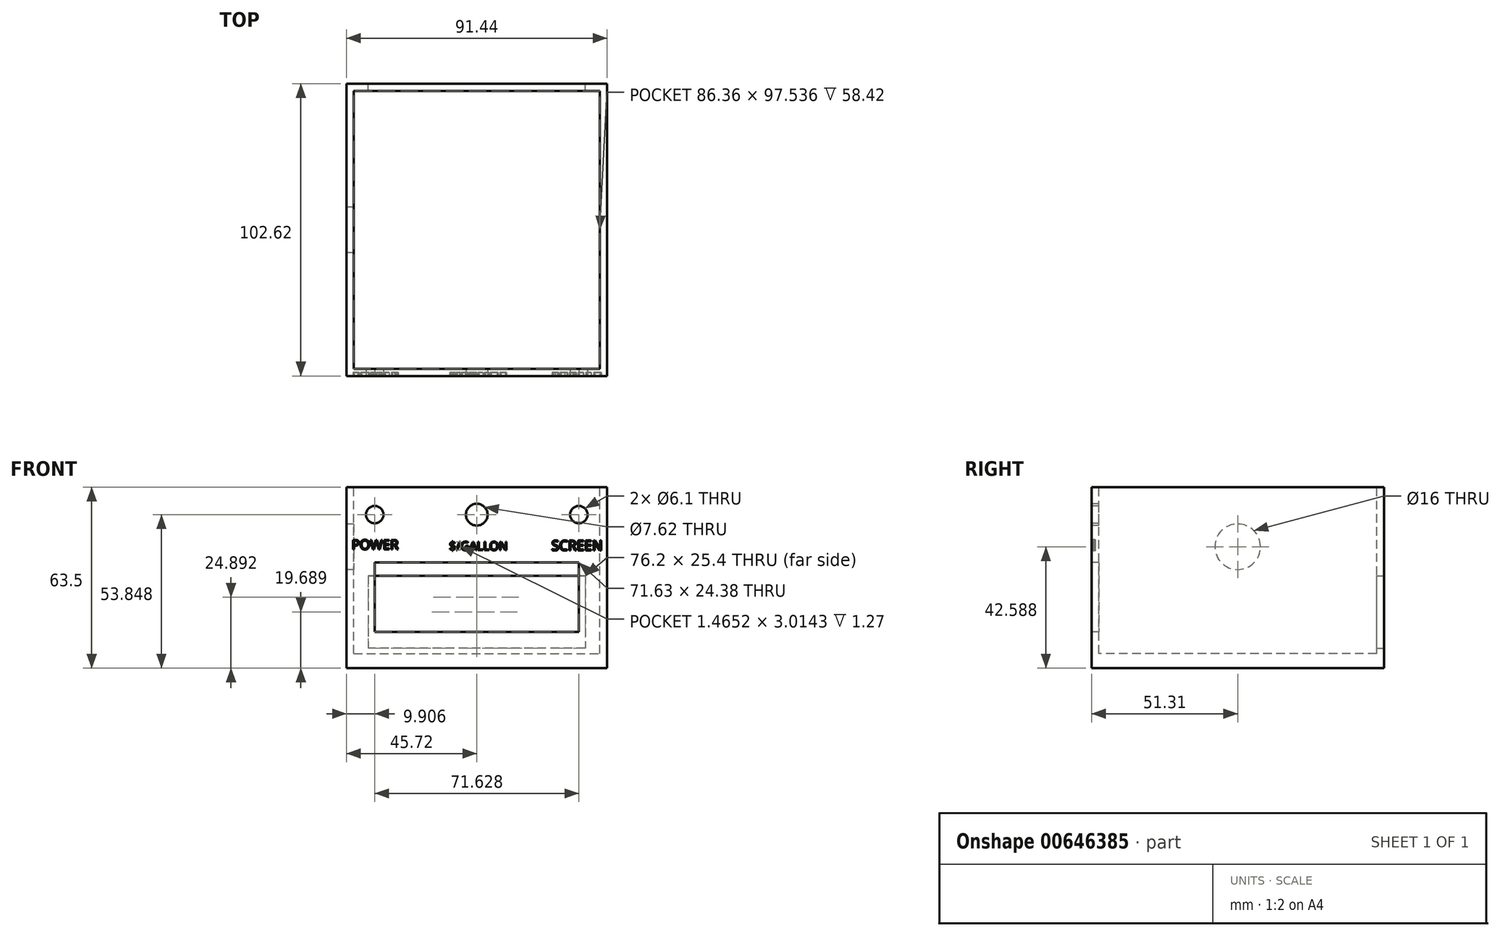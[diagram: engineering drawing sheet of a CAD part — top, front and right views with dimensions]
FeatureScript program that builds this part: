
annotation { "Feature Type Name" : "Feature", "Feature Type Description" : "" }
export const myFeature = defineFeature(function(context is Context, id is Id, definition is map)
    precondition{}
    {
        {
            var Q0;
            Q0=qCreatedBy(makeId("Top.planeOp"),FACE);
            var sketch = newSketch(context, id + "F0", { "sketchPlane" : qUnion([Q0])});
            skLineSegment(sketch, "E0.bottom", {"start": v(-45.72, 51.3) * mm, "end": v(45.72, 51.3) * mm});
            skLineSegment(sketch, "E0.top", {"start": v(-45.72, -51.3) * mm, "end": v(45.72, -51.3) * mm});
            skLineSegment(sketch, "E0.left", {"start": v(-45.72, 51.3) * mm, "end": v(-45.72, -51.3) * mm});
            skLineSegment(sketch, "E0.right", {"start": v(45.72, 51.3) * mm, "end": v(45.72, -51.3) * mm});
            skSolve(sketch);
        }
        {
            var Q0;
            Q0=makeQuery(id+"F0.imprint","IMPRINT",FACE,{"disambiguationData":[TD([[makeQuery(id+"F0.imprint","IMPRINT",EDGE,{"derivedFrom":sQuery(id+"F0.wireOp",EDGE,"E0.bottom")}),-1.0]])]});
            extrude(context, id + "F1", {"entities" : qUnion([Q0]), "depth" : 63.5 * mm, "offsetDistance" : 25.4 * mm});
        }
        {
            var Q0;
            Q0=makeQuery(id+"F1.opExtrude","CAP_FACE",FACE,{"disambiguationData":[OSD([sQuery(id+"F0.wireOp",EDGE,"E0.bottom"),sQuery(id+"F0.wireOp",EDGE,"E0.top"),sQuery(id+"F0.wireOp",EDGE,"E0.left"),sQuery(id+"F0.wireOp",EDGE,"E0.right")])],"isStart":false});
            var sketch = newSketch(context, id + "F2", { "sketchPlane" : qUnion([Q0])});
            skLineSegment(sketch, "E1.bottom", {"start": v(-43.18, 48.77) * mm, "end": v(43.18, 48.77) * mm});
            skLineSegment(sketch, "E1.top", {"start": v(-43.18, -48.77) * mm, "end": v(43.18, -48.77) * mm});
            skLineSegment(sketch, "E1.left", {"start": v(-43.18, 48.77) * mm, "end": v(-43.18, -48.77) * mm});
            skLineSegment(sketch, "E1.right", {"start": v(43.18, 48.77) * mm, "end": v(43.18, -48.77) * mm});
            skSolve(sketch);
        }
        {
            var Q0;
            Q0=makeQuery(id+"F2.imprint","IMPRINT",FACE,{"disambiguationData":[TD([[makeQuery(id+"F2.imprint","IMPRINT",EDGE,{"derivedFrom":sQuery(id+"F2.wireOp",EDGE,"E1.bottom")}),-1.0]])]});
            extrude(context, id + "F3", {"entities" : qUnion([Q0]), "operationType" : NewBodyOperationType.REMOVE, "oppositeDirection" : true, "depth" : 58.42 * mm, "offsetDistance" : 25.4 * mm});
        }
        {
            var Q0;
            Q0=makeQuery(id+"F1.opExtrude","SWEPT_FACE",FACE,{"disambiguationData":[OSD([sQuery(id+"F0.wireOp",EDGE,"E0.top")])]});
            var sketch = newSketch(context, id + "F4", { "sketchPlane" : qUnion([Q0])});
            skLineSegment(sketch, "E2.bottom", {"start": v(-35.81, 37.08) * mm, "end": v(35.81, 37.08) * mm});
            skLineSegment(sketch, "E2.top", {"start": v(-35.81, 12.7) * mm, "end": v(35.81, 12.7) * mm});
            skLineSegment(sketch, "E2.left", {"start": v(-35.81, 37.08) * mm, "end": v(-35.81, 12.7) * mm});
            skLineSegment(sketch, "E2.right", {"start": v(35.81, 37.08) * mm, "end": v(35.81, 12.7) * mm});
            skSolve(sketch);
        }
        {
            var Q0;
            Q0=makeQuery(id+"F4.imprint","IMPRINT",FACE,{"disambiguationData":[TD([[makeQuery(id+"F4.imprint","IMPRINT",EDGE,{"derivedFrom":sQuery(id+"F4.wireOp",EDGE,"E2.bottom")}),-1.0]])]});
            extrude(context, id + "F5", {"entities" : qUnion([Q0]), "operationType" : NewBodyOperationType.REMOVE, "oppositeDirection" : true, "depth" : 25.4 * mm, "offsetDistance" : 25.4 * mm});
        }
        {
            var Q0;
            Q0=makeQuery(id+"F1.opExtrude","SWEPT_FACE",FACE,{"disambiguationData":[OSD([sQuery(id+"F0.wireOp",EDGE,"E0.top")])]});
            var sketch = newSketch(context, id + "F6", { "sketchPlane" : qUnion([Q0])});
            skCircle(sketch, "E3", {"center": v(0, 53.85) * mm, "radius": 3.81 * mm});
            skPoint(sketch, "E3.centerSnap0", {"position": v(0, 37.08) * mm});
            skCircle(sketch, "E4", {"center": v(-35.81, 53.85) * mm, "radius": 3.05 * mm});
            skCircle(sketch, "E5", {"center": v(35.81, 53.85) * mm, "radius": 3.05 * mm});
            skSolve(sketch);
        }
        {
            var Q0;
            Q0=makeQuery(id+"F6.imprint","IMPRINT",FACE,{"disambiguationData":[TD([[makeQuery(id+"F6.imprint","IMPRINT",EDGE,{"derivedFrom":sQuery(id+"F6.wireOp",EDGE,"E4")}),1.0]])]});
            var Q1;
            Q1=makeQuery(id+"F6.imprint","IMPRINT",FACE,{"disambiguationData":[TD([[makeQuery(id+"F6.imprint","IMPRINT",EDGE,{"derivedFrom":sQuery(id+"F6.wireOp",EDGE,"E3")}),1.0]])]});
            var Q2;
            Q2=makeQuery(id+"F6.imprint","IMPRINT",FACE,{"disambiguationData":[TD([[makeQuery(id+"F6.imprint","IMPRINT",EDGE,{"derivedFrom":sQuery(id+"F6.wireOp",EDGE,"E5")}),1.0]])]});
            extrude(context, id + "F7", {"entities" : qUnion([Q0, Q1, Q2]), "operationType" : NewBodyOperationType.REMOVE, "oppositeDirection" : true, "depth" : 7.62 * mm, "offsetDistance" : 25.4 * mm});
        }
        {
            var Q0;
            Q0=makeQuery(id+"F1.opExtrude","SWEPT_FACE",FACE,{"disambiguationData":[OSD([sQuery(id+"F0.wireOp",EDGE,"E0.top")])]});
            var sketch = newSketch(context, id + "F8", { "sketchPlane" : qUnion([Q0])});
            skText(sketch, "E6", { "text": "POWER", "fontName": "OpenSans-Regular.ttf"});
            const initialGuessF8  = {"E6": [-0.04393, 0.04162, 1, 0, 0.0034]};
            skSetInitialGuess(sketch, initialGuessF8);
            skSolve(sketch);
        }
        {
            var Q0;
            Q0 = qSketchRegion(id + "F8", true);
            extrude(context, id + "F9", {"entities" : qUnion([Q0]), "operationType" : NewBodyOperationType.REMOVE, "oppositeDirection" : true, "depth" : 1.27 * mm, "offsetDistance" : 25.4 * mm});
        }
        {
            var Q0;
            {var subQ1=sQuery(id+"F0.wireOp",EDGE,"E0.left");var subQ2=sQuery(id+"F0.wireOp",EDGE,"E0.top");Q0=makeQuery(id+"F9.boolean.opBoolean","SPLIT",FACE,{"disambiguationData":[TD([makeQuery(id+"F1.opExtrude","SWEPT_FACE",FACE,{"disambiguationData":[OSD([subQ1])]})])],"derivedFrom":makeQuery(id+"F1.opExtrude","SWEPT_FACE",FACE,{"disambiguationData":[OSD([subQ2])]})});}
            var sketch = newSketch(context, id + "F10", { "sketchPlane" : qUnion([Q0])});
            skText(sketch, "E7", { "text": "$/GALLON", "fontName": "OpenSans-Regular.ttf"});
            const initialGuessF10  = {"E7": [-0.00968, 0.04134, 1, 0, 0.00304]};
            skSetInitialGuess(sketch, initialGuessF10);
            skSolve(sketch);
        }
        {
            var Q0;
            Q0 = qSketchRegion(id + "F10", true);
            extrude(context, id + "F11", {"entities" : qUnion([Q0]), "operationType" : NewBodyOperationType.REMOVE, "oppositeDirection" : true, "depth" : 1.27 * mm, "offsetDistance" : 25.4 * mm});
        }
        {
            var Q0;
            {var subQ26=sQuery(id+"F0.wireOp",EDGE,"E0.left");var subQ27=makeQuery(id+"F1.opExtrude","SWEPT_FACE",FACE,{"disambiguationData":[OSD([subQ26])]});var subQ30=sQuery(id+"F0.wireOp",EDGE,"E0.top");Q0=makeQuery(id+"F11.boolean.opBoolean","SPLIT",FACE,{"disambiguationData":[TD([subQ27])],"derivedFrom":makeQuery(id+"F9.boolean.opBoolean","SPLIT",FACE,{"disambiguationData":[TD([subQ27])],"derivedFrom":makeQuery(id+"F1.opExtrude","SWEPT_FACE",FACE,{"disambiguationData":[OSD([subQ30])]})})});}
            var sketch = newSketch(context, id + "F12", { "sketchPlane" : qUnion([Q0])});
            skText(sketch, "E8", { "text": "SCREEN", "fontName": "OpenSans-Regular.ttf"});
            const initialGuessF12  = {"E8": [0.02622, 0.04127, 1, 0, 0.00353]};
            skSetInitialGuess(sketch, initialGuessF12);
            skSolve(sketch);
        }
        {
            var Q0;
            Q0 = qSketchRegion(id + "F12", true);
            extrude(context, id + "F13", {"entities" : qUnion([Q0]), "operationType" : NewBodyOperationType.REMOVE, "oppositeDirection" : true, "depth" : 1.27 * mm, "offsetDistance" : 25.4 * mm});
        }
        {
            var Q0;
            Q0=makeQuery(id+"F1.opExtrude","SWEPT_FACE",FACE,{"disambiguationData":[OSD([sQuery(id+"F0.wireOp",EDGE,"E0.left")])]});
            var sketch = newSketch(context, id + "F14", { "sketchPlane" : qUnion([Q0])});
            skCircle(sketch, "E9", {"center": v(0, 42.59) * mm, "radius": 8 * mm});
            skSolve(sketch);
        }
        {
            var Q0;
            Q0=makeQuery(id+"F14.imprint","IMPRINT",FACE,{"disambiguationData":[TD([[makeQuery(id+"F14.imprint","IMPRINT",EDGE,{"derivedFrom":sQuery(id+"F14.wireOp",EDGE,"E9")}),1.0]])]});
            extrude(context, id + "F15", {"entities" : qUnion([Q0]), "operationType" : NewBodyOperationType.REMOVE, "oppositeDirection" : true, "depth" : 7.62 * mm, "offsetDistance" : 25.4 * mm});
        }
        {
            var Q0;
            {var subQ168=sQuery(id+"F0.wireOp",EDGE,"E0.left");var subQ169=sQuery(id+"F0.wireOp",EDGE,"E0.top");var subQ181=makeQuery(id+"F1.opExtrude","SWEPT_FACE",FACE,{"disambiguationData":[OSD([subQ168])]});Q0=makeQuery(id+"F13.boolean.opBoolean","SPLIT",FACE,{"disambiguationData":[TD([subQ181])],"derivedFrom":makeQuery(id+"F11.boolean.opBoolean","SPLIT",FACE,{"disambiguationData":[TD([subQ181])],"derivedFrom":makeQuery(id+"F9.boolean.opBoolean","SPLIT",FACE,{"disambiguationData":[TD([subQ181])],"derivedFrom":makeQuery(id+"F1.opExtrude","SWEPT_FACE",FACE,{"disambiguationData":[OSD([subQ169])]})})})});}
            var sketch = newSketch(context, id + "F16", { "sketchPlane" : qUnion([Q0])});
            skCircle(sketch, "E10", {"center": v(-37, 40.13) * mm, "radius": 1.27 * mm});
            skCircle(sketch, "E11", {"center": v(37.94, 40.13) * mm, "radius": 1.27 * mm});
            skCircle(sketch, "E12", {"center": v(37.94, 9.65) * mm, "radius": 1.27 * mm});
            skCircle(sketch, "E13", {"center": v(-37, 9.65) * mm, "radius": 1.27 * mm});
            skSolve(sketch);
        }
        {
            var Q0;
            Q0=makeQuery(id+"F1.opExtrude","SWEPT_FACE",FACE,{"disambiguationData":[OSD([sQuery(id+"F0.wireOp",EDGE,"E0.left")])]});
            var sketch = newSketch(context, id + "F17", { "sketchPlane" : qUnion([Q0])});
            skLineSegment(sketch, "E14.bottom", {"start": v(-25.9, 63.5) * mm, "end": v(-13.2, 63.5) * mm});
            skLineSegment(sketch, "E14.top", {"start": v(-25.9, 57.15) * mm, "end": v(-13.2, 57.15) * mm});
            skLineSegment(sketch, "E14.left", {"start": v(-25.9, 63.5) * mm, "end": v(-25.9, 57.15) * mm});
            skLineSegment(sketch, "E14.right", {"start": v(-13.2, 63.5) * mm, "end": v(-13.2, 57.15) * mm});
            skLineSegment(sketch, "E15.bottom", {"start": v(24.9, 63.5) * mm, "end": v(37.6, 63.5) * mm});
            skLineSegment(sketch, "E15.top", {"start": v(24.9, 57.15) * mm, "end": v(37.6, 57.15) * mm});
            skLineSegment(sketch, "E15.left", {"start": v(24.9, 63.5) * mm, "end": v(24.9, 57.15) * mm});
            skLineSegment(sketch, "E15.right", {"start": v(37.6, 63.5) * mm, "end": v(37.6, 57.15) * mm});
            skSolve(sketch);
        }
        {
            var Q0;
            Q0=makeQuery(id+"F1.opExtrude","SWEPT_FACE",FACE,{"disambiguationData":[OSD([sQuery(id+"F0.wireOp",EDGE,"E0.bottom")])]});
            var sketch = newSketch(context, id + "F18", { "sketchPlane" : qUnion([Q0])});
            skLineSegment(sketch, "E16.bottom", {"start": v(-38.1, 32.39) * mm, "end": v(38.1, 32.39) * mm});
            skLineSegment(sketch, "E16.top", {"start": v(-38.1, 6.99) * mm, "end": v(38.1, 6.99) * mm});
            skLineSegment(sketch, "E16.left", {"start": v(-38.1, 32.39) * mm, "end": v(-38.1, 6.99) * mm});
            skLineSegment(sketch, "E16.right", {"start": v(38.1, 32.39) * mm, "end": v(38.1, 6.99) * mm});
            skSolve(sketch);
        }
        {
            var Q0;
            Q0=makeQuery(id+"F18.imprint","IMPRINT",FACE,{"disambiguationData":[TD([[makeQuery(id+"F18.imprint","IMPRINT",EDGE,{"derivedFrom":sQuery(id+"F18.wireOp",EDGE,"E16.bottom")}),-1.0]])]});
            extrude(context, id + "F19", {"entities" : qUnion([Q0]), "operationType" : NewBodyOperationType.REMOVE, "oppositeDirection" : true, "depth" : 25.4 * mm, "offsetDistance" : 25.4 * mm});
        }
    });
